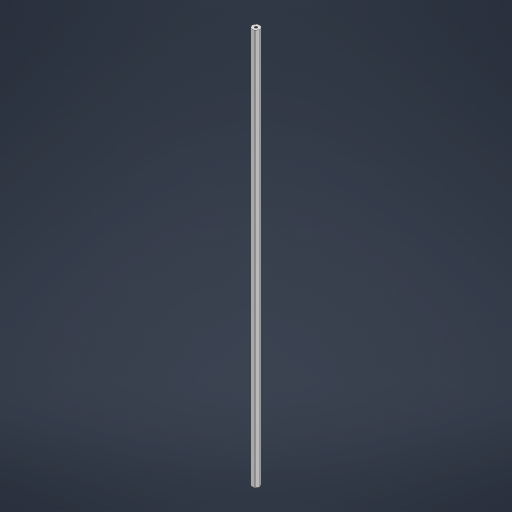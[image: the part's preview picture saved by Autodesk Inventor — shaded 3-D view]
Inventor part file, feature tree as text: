
AUTODESK INVENTOR PART (.ipt)
format: ipt  version: 2023 (Build 270158000, 158)  size: 739,840 bytes
history: native  units: in
note: dims shown in document units (in); Inventor stores cm internally (conversion verified against a paired STEP export)
features: mirror x1
ambient origin geometry x8: Origin, YZ Plane, XZ Plane, XY Plane, X Axis, Y Axis, Z Axis, Center Point
bodies: Solid1 (feature_tree)
feature tree (1):
  mirror  "Mirror2"
